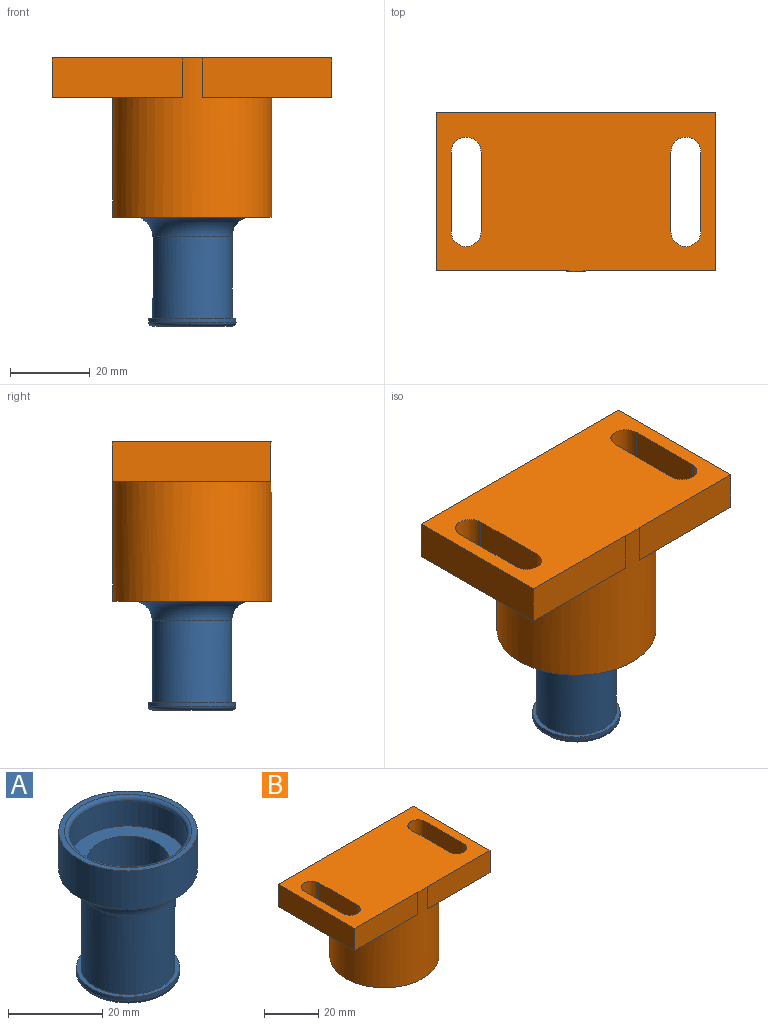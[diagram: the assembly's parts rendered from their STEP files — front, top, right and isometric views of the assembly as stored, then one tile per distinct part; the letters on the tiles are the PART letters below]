
ASSEMBLY  parts=2 mates=1
PART A: 12 faces, bbox 32.6x32.6x37.5 mm
  f0: cylinder r=10mm len=20.43mm, axis (0,0,1), area 1283.7mm2, adj f6,f8
  f1: cylinder r=14.75mm len=29.5mm, axis (0,0,-1), area 926.8mm2, adj f2,f6
  f2: plane 29.5x29.5mm, normal (0,0,1), area 110.9mm2, adj f1,f5
  f3: cylinder r=12.5mm len=25mm, axis (0,0,1), area 510.5mm2, adj f4,f5
  f4: plane 25x25mm, normal (0,0,1), area 250.3mm2, adj f3,f10
  f5: torus R=13.5mm, axis (0,0,1), area 127mm2, adj f2,f3
  f6: torus R=15.08mm, axis (0,0,1), area 563mm2, adj f0,f1
  f7: cylinder r=11mm len=22mm, axis (0,0,-1), area 69.1mm2, adj f8,f11
  f8: plane 22x22mm, normal (0,0,1), area 66mm2, adj f0,f7
  f9: plane 20x20mm, normal (0,0,-1), area 73.6mm2, adj f10,f11
  f10: cylinder r=8.75mm len=30mm, axis (0,0,1), area 1649.3mm2, adj f4,f9
  f11: torus R=10mm, axis (0,0,1), area 105mm2, adj f7,f9
PART B: 21 faces, bbox 70.3x40x40 mm
  f0: cylinder r=15mm len=30mm, axis (0,0,-1), area 2638.9mm2, adj f4,f20
  f1: cylinder r=20mm len=40mm, axis (0,0,-1), area 3819.4mm2, adj f2,f3,f5,f6,f8,f9
  f2: plane 70.26x40mm, normal (0,0,1), area 2411.8mm2, adj f1,f5,f6,f7,f10,f11,f12,f13
  f3: plane 40x40mm, normal (0,0,-1), area 348.7mm2, adj f1,f20
  f4: plane 30x30mm, normal (0,0,-1), area 706.9mm2, adj f0
  f5: plane 32.73x10mm, normal (0,-1,0), area 327.3mm2, adj f1,f2,f8,f10
  f6: plane 32.6x10mm, normal (0,-1,0), area 326mm2, adj f1,f2,f9,f11
  f7: plane 70.26x10mm, normal (0,1,0), area 702.6mm2, adj f2,f8,f9,f10,f11
  f8: plane 39.85x35.19mm, normal (0,0,-1), area 580.1mm2, adj f1,f5,f7,f10,f16,f17,f18,f19
  f9: plane 39.85x35.07mm, normal (0,0,-1), area 575mm2, adj f1,f6,f7,f11,f12,f13,f14,f15
  f10: plane 39.85x10mm, normal (-1,0,0), area 398.5mm2, adj f2,f5,f7,f8
  f11: plane 39.85x10mm, normal (1,0,0), area 398.5mm2, adj f2,f6,f7,f9
  f12: cylinder r=3.75mm len=10mm, axis (0,0,-1), area 117.8mm2, adj f2,f9,f13,f15
  f13: plane 20x10mm, normal (1,0,0), area 200mm2, adj f2,f9,f12,f14
  f14: cylinder r=3.75mm len=10mm, axis (0,0,-1), area 117.8mm2, adj f2,f9,f13,f15
  f15: plane 20x10mm, normal (-1,0,0), area 200mm2, adj f2,f9,f12,f14
  f16: cylinder r=3.75mm len=10mm, axis (0,0,-1), area 117.8mm2, adj f2,f8,f17,f19
  f17: plane 20x10mm, normal (1,0,0), area 200mm2, adj f2,f8,f16,f18
  f18: cylinder r=3.75mm len=10mm, axis (0,0,-1), area 117.8mm2, adj f2,f8,f17,f19
  f19: plane 20x10mm, normal (-1,0,0), area 200mm2, adj f2,f8,f16,f18
  f20: torus R=17mm, axis (0,0,1), area 310.4mm2, adj f0,f3
PLACE A t=(-38.78,-5.05,-0.04)mm
PLACE B t=(-38.78,-5.05,-0.14)mm
MATE slider B.f0 <-> A.f1  axis (0,0,1) through (-38.78,-5.05,-0.14)mm
